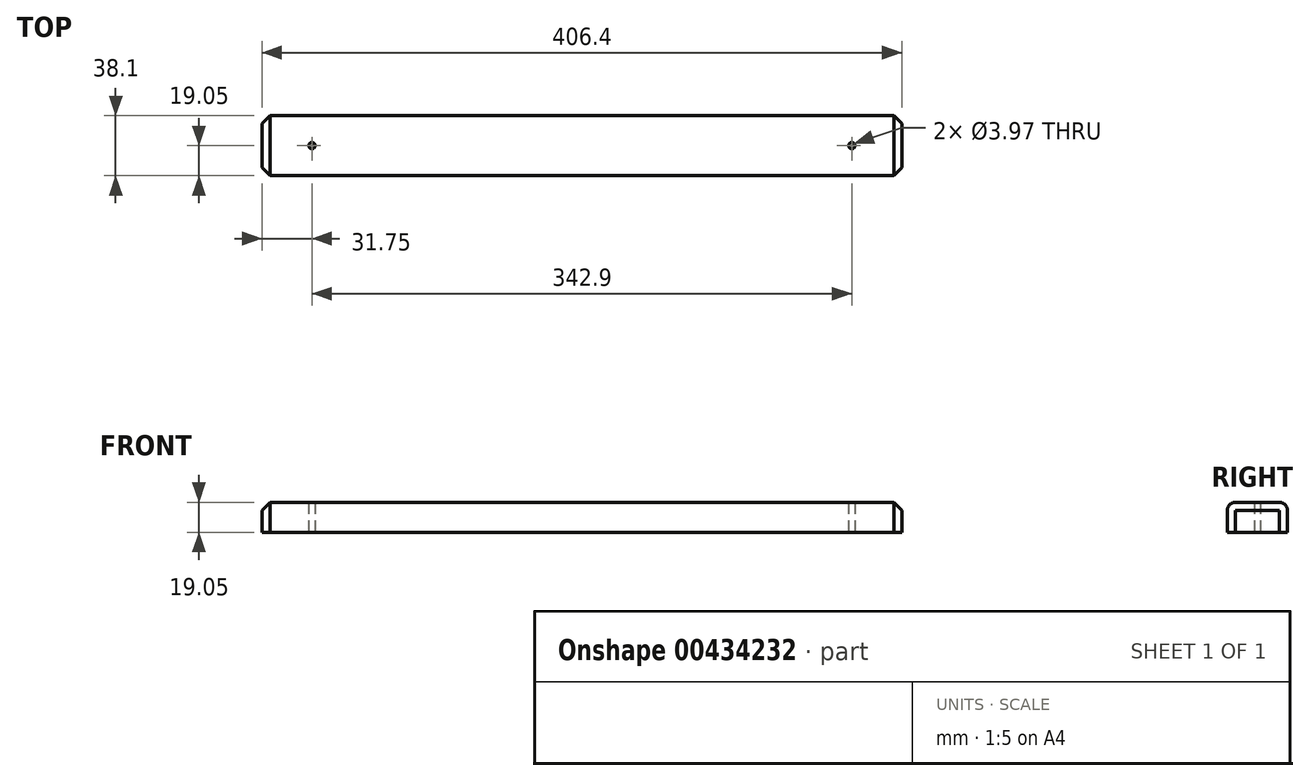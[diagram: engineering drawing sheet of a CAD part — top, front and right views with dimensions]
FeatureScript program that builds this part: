
annotation { "Feature Type Name" : "Feature", "Feature Type Description" : "" }
export const myFeature = defineFeature(function(context is Context, id is Id, definition is map)
    precondition{}
    {
        {
            var Q0;
            Q0=qCreatedBy(makeId("Right.planeOp"),FACE);
            var sketch = newSketch(context, id + "F0", { "sketchPlane" : qUnion([Q0])});
            skLineSegment(sketch, "E0.bottom", {"start": v(0, 0) * mm, "end": v(38.1, 0) * mm});
            skLineSegment(sketch, "E0.top", {"start": v(0, 19.05) * mm, "end": v(38.1, 19.05) * mm});
            skLineSegment(sketch, "E0.left", {"start": v(0, 0) * mm, "end": v(0, 19.05) * mm});
            skLineSegment(sketch, "E0.right", {"start": v(38.1, 0) * mm, "end": v(38.1, 19.05) * mm});
            skSolve(sketch);
        }
        {
            var Q0;
            Q0 = qSketchRegion(id + "F0", true);
            extrude(context, id + "F1", {"entities" : qUnion([Q0]), "depth" : 406.4 * mm});
        }
        {
            var Q0;
            Q0=makeQuery(id+"F1.opExtrude","SWEPT_EDGE",EDGE,{"disambiguationData":[OSD([sQuery(id+"F0.wireOp",EDGE,"E0.top"),sQuery(id+"F0.wireOp",EDGE,"E0.left")])]});
            var Q1;
            Q1=makeQuery(id+"F1.opExtrude","SWEPT_EDGE",EDGE,{"disambiguationData":[OSD([sQuery(id+"F0.wireOp",EDGE,"E0.top"),sQuery(id+"F0.wireOp",EDGE,"E0.right")])]});
            fillet(context, id + "F2", {"entities" : qUnion([Q0, Q1]), "radius" : 5.08 * mm, "tangentPropagation" : true, "allowEdgeOverflow" : false});
        }
        {
            var Q0;
            Q0=makeQuery(id+"F1.opExtrude","CAP_EDGE",EDGE,{"disambiguationData":[OSD([sQuery(id+"F0.wireOp",EDGE,"E0.top")])],"isStart":false});
            var Q1;
            Q1=makeQuery(id+"F1.opExtrude","CAP_EDGE",EDGE,{"disambiguationData":[OSD([sQuery(id+"F0.wireOp",EDGE,"E0.top")])],"isStart":true});
            chamfer(context, id + "F3", {"entities" : qUnion([Q0, Q1]), "width" : 5.08 * mm, "tangentPropagation" : true});
        }
        {
            var Q0;
            Q0=makeQuery(id+"F1.opExtrude","SWEPT_FACE",FACE,{"disambiguationData":[OSD([sQuery(id+"F0.wireOp",EDGE,"E0.bottom")])]});
            var sketch = newSketch(context, id + "F4", { "sketchPlane" : qUnion([Q0])});
            skCircle(sketch, "E1", {"center": v(31.75, -19.05) * mm, "radius": 1.98 * mm});
            skLineSegment(sketch, "E2", {"start": v(203.2, 12.96) * mm, "end": v(203.2, -63.34) * mm, "construction": true});
            skPoint(sketch, "E2.startSnap0", {"position": v(203.2, 0) * mm});
            skCircle(sketch, "E3.MirrorC", {"center": v(374.65, -19.05) * mm, "radius": 1.98 * mm});
            skSolve(sketch);
        }
        {
            var Q0;
            Q0 = qSketchRegion(id + "F4", true);
            extrude(context, id + "F5", {"entities" : qUnion([Q0]), "operationType" : NewBodyOperationType.REMOVE, "oppositeDirection" : true, "depth" : 25.4 * mm});
        }
    });
